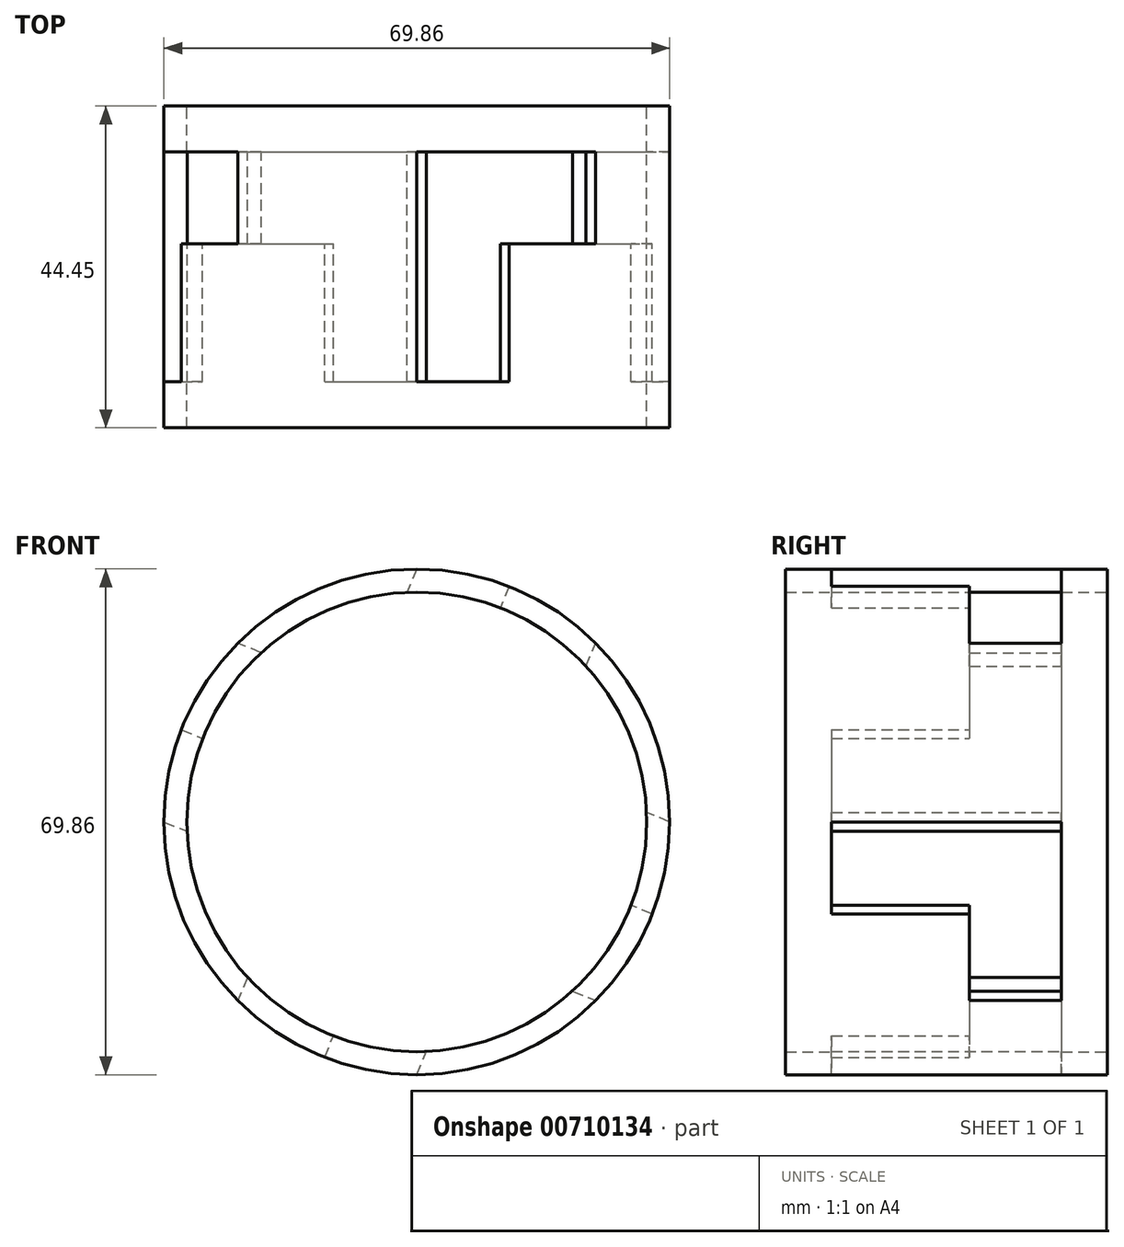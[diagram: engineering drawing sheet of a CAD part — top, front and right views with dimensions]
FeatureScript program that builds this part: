
annotation { "Feature Type Name" : "Feature", "Feature Type Description" : "" }
export const myFeature = defineFeature(function(context is Context, id is Id, definition is map)
    precondition{}
    {
        {
            var Q0;
            Q0=qCreatedBy(makeId("Front.planeOp"),FACE);
            var sketch = newSketch(context, id + "F0", { "sketchPlane" : qUnion([Q0])});
            skCircle(sketch, "E0", {"center": v(0, 0) * mm, "radius": 31.75 * mm});
            skCircle(sketch, "E1", {"center": v(0, 0) * mm, "radius": 34.93 * mm});
            skSolve(sketch);
        }
        {
            var Q0;
            Q0=makeQuery(id+"F0.imprint","IMPRINT",FACE,{"disambiguationData":[TD([[makeQuery(id+"F0.imprint","IMPRINT",EDGE,{"derivedFrom":sQuery(id+"F0.wireOp",EDGE,"E0")}),-1.0]])]});
            extrude(context, id + "F1", {"entities" : qUnion([Q0]), "depth" : 44.45 * mm, "offsetDistance" : 25.4 * mm});
        }
        {
            var Q0;
            Q0=qCreatedBy(makeId("Top.planeOp"),FACE);
            cPlane(context, id + "F2", {"entities" : qUnion([Q0]), "cplaneType" : CPlaneType.OFFSET, "offset" : 38.1 * mm, "width" : 152.4 * mm, "height" : 152.4 * mm});
        }
        {
            var Q0;
            Q0=qCreatedBy(makeId("Front.planeOp"),FACE);
            cPlane(context, id + "F3", {"entities" : qUnion([Q0]), "cplaneType" : CPlaneType.OFFSET, "offset" : 6.35 * mm, "width" : 152.4 * mm, "height" : 152.4 * mm});
        }
        {
            var Q0;
            Q0=qCreatedBy(id+"F3.planeOp",FACE);
            var sketch = newSketch(context, id + "F4", { "sketchPlane" : qUnion([Q0])});
            skLineSegment(sketch, "E2.0", {"start": v(1.22, 37.86) * mm, "end": v(25.91, 27.63) * mm});
            skLineSegment(sketch, "E3.0", {"start": v(-2.43, 29.06) * mm, "end": v(22.27, 18.83) * mm});
            skLineSegment(sketch, "E4", {"start": v(1.22, 37.86) * mm, "end": v(-2.43, 29.06) * mm});
            skLineSegment(sketch, "E5", {"start": v(22.27, 18.83) * mm, "end": v(25.91, 27.63) * mm});
            skLineSegment(sketch, "E6.1.0", {"start": v(-18.83, 22.27) * mm, "end": v(-27.63, 25.91) * mm});
            skLineSegment(sketch, "E6.1.1", {"start": v(-37.86, 1.22) * mm, "end": v(-27.63, 25.91) * mm});
            skLineSegment(sketch, "E6.1.2", {"start": v(-37.86, 1.22) * mm, "end": v(-29.06, -2.43) * mm});
            skLineSegment(sketch, "E6.1.3", {"start": v(-29.06, -2.43) * mm, "end": v(-18.83, 22.27) * mm});
            skLineSegment(sketch, "E6.2.0", {"start": v(-22.27, -18.83) * mm, "end": v(-25.91, -27.63) * mm});
            skLineSegment(sketch, "E6.2.1", {"start": v(-1.22, -37.86) * mm, "end": v(-25.91, -27.63) * mm});
            skLineSegment(sketch, "E6.2.2", {"start": v(-1.22, -37.86) * mm, "end": v(2.43, -29.06) * mm});
            skLineSegment(sketch, "E6.2.3", {"start": v(2.43, -29.06) * mm, "end": v(-22.27, -18.83) * mm});
            skLineSegment(sketch, "E6.3.0", {"start": v(18.83, -22.27) * mm, "end": v(27.63, -25.91) * mm});
            skLineSegment(sketch, "E6.3.1", {"start": v(37.86, -1.22) * mm, "end": v(27.63, -25.91) * mm});
            skLineSegment(sketch, "E6.3.2", {"start": v(37.86, -1.22) * mm, "end": v(29.06, 2.43) * mm});
            skLineSegment(sketch, "E6.3.3", {"start": v(29.06, 2.43) * mm, "end": v(18.83, -22.27) * mm});
            skPoint(sketch, "E6.center", {"position": v(0, 0) * mm});
            skSolve(sketch);
        }
        {
            var Q0;
            Q0=makeQuery(id+"F4.imprint","IMPRINT",FACE,{"disambiguationData":[TD([[makeQuery(id+"F4.imprint","IMPRINT",EDGE,{"derivedFrom":sQuery(id+"F4.wireOp",EDGE,"E6.1.0")}),1.0]])]});
            var Q1;
            Q1=makeQuery(id+"F4.imprint","IMPRINT",FACE,{"disambiguationData":[TD([[makeQuery(id+"F4.imprint","IMPRINT",EDGE,{"derivedFrom":sQuery(id+"F4.wireOp",EDGE,"E2.0")}),-1.0]])]});
            var Q2;
            Q2=makeQuery(id+"F4.imprint","IMPRINT",FACE,{"disambiguationData":[TD([[makeQuery(id+"F4.imprint","IMPRINT",EDGE,{"derivedFrom":sQuery(id+"F4.wireOp",EDGE,"E6.3.0")}),1.0]])]});
            var Q3;
            Q3=makeQuery(id+"F4.imprint","IMPRINT",FACE,{"disambiguationData":[TD([[makeQuery(id+"F4.imprint","IMPRINT",EDGE,{"derivedFrom":sQuery(id+"F4.wireOp",EDGE,"E6.2.0")}),1.0]])]});
            extrude(context, id + "F5", {"entities" : qUnion([Q0, Q1, Q2, Q3]), "operationType" : NewBodyOperationType.REMOVE, "depth" : 12.7 * mm, "offsetDistance" : 25.4 * mm});
        }
        {
            var Q0;
            Q0=qCreatedBy(id+"F3.planeOp",FACE);
            cPlane(context, id + "F6", {"entities" : qUnion([Q0]), "cplaneType" : CPlaneType.OFFSET, "offset" : 12.7 * mm, "width" : 152.4 * mm, "height" : 152.4 * mm});
        }
        {
            var Q0;
            Q0=qCreatedBy(id+"F6.planeOp",FACE);
            var sketch = newSketch(context, id + "F7", { "sketchPlane" : qUnion([Q0])});
            skCircle(sketch, "E7.cCircle", {"center": v(0, 0) * mm, "radius": 34.93 * mm, "construction": true});
            skLineSegment(sketch, "E7.1", {"start": v(24.7, 24.7) * mm, "end": v(34.93, 0) * mm});
            skLineSegment(sketch, "E7.3", {"start": v(24.7, -24.7) * mm, "end": v(0, -34.93) * mm});
            skLineSegment(sketch, "E7.5", {"start": v(-24.7, -24.7) * mm, "end": v(-34.93, 0) * mm});
            skLineSegment(sketch, "E7.7", {"start": v(-24.7, 24.7) * mm, "end": v(0, 34.93) * mm});
            skLineSegment(sketch, "E8.0", {"start": v(-2.43, 29.06) * mm, "end": v(9.3, 24.2) * mm});
            skLineSegment(sketch, "E9.0", {"start": v(1.22, 37.86) * mm, "end": v(12.95, 33) * mm});
            skLineSegment(sketch, "E10", {"start": v(1.22, 37.86) * mm, "end": v(-2.43, 29.06) * mm});
            skLineSegment(sketch, "E11.0", {"start": v(12.95, 33) * mm, "end": v(9.3, 24.2) * mm});
            skLineSegment(sketch, "E12.1.0", {"start": v(-29.06, -2.43) * mm, "end": v(-24.2, 9.3) * mm});
            skLineSegment(sketch, "E12.1.1", {"start": v(-33, 12.95) * mm, "end": v(-24.2, 9.3) * mm});
            skLineSegment(sketch, "E12.1.2", {"start": v(-37.86, 1.22) * mm, "end": v(-29.06, -2.43) * mm});
            skLineSegment(sketch, "E12.1.3", {"start": v(-37.86, 1.22) * mm, "end": v(-33, 12.95) * mm});
            skLineSegment(sketch, "E12.2.0", {"start": v(2.43, -29.06) * mm, "end": v(-9.3, -24.2) * mm});
            skLineSegment(sketch, "E12.2.1", {"start": v(-12.95, -33) * mm, "end": v(-9.3, -24.2) * mm});
            skLineSegment(sketch, "E12.2.2", {"start": v(-1.22, -37.86) * mm, "end": v(2.43, -29.06) * mm});
            skLineSegment(sketch, "E12.2.3", {"start": v(-1.22, -37.86) * mm, "end": v(-12.95, -33) * mm});
            skLineSegment(sketch, "E12.3.0", {"start": v(29.06, 2.43) * mm, "end": v(24.2, -9.3) * mm});
            skLineSegment(sketch, "E12.3.1", {"start": v(33, -12.95) * mm, "end": v(24.2, -9.3) * mm});
            skLineSegment(sketch, "E12.3.2", {"start": v(37.86, -1.22) * mm, "end": v(29.06, 2.43) * mm});
            skLineSegment(sketch, "E12.3.3", {"start": v(37.86, -1.22) * mm, "end": v(33, -12.95) * mm});
            skSolve(sketch);
        }
        {
            var Q0;
            {var subQ2=sQuery(id+"F7.wireOp",EDGE,"E8.0");Q0=makeQuery(id+"F7.imprint","IMPRINT",FACE,{"disambiguationData":[TD([[makeQuery(id+"F7.imprint","IMPRINT",EDGE,{"derivedFrom":subQ2}),1.0]])]});}
            var Q1;
            {var subQ2=sQuery(id+"F7.wireOp",EDGE,"E12.1.0");Q1=makeQuery(id+"F7.imprint","IMPRINT",FACE,{"disambiguationData":[TD([[makeQuery(id+"F7.imprint","IMPRINT",EDGE,{"derivedFrom":subQ2}),1.0]])]});}
            var Q2;
            {var subQ2=sQuery(id+"F7.wireOp",EDGE,"E12.2.0");Q2=makeQuery(id+"F7.imprint","IMPRINT",FACE,{"disambiguationData":[TD([[makeQuery(id+"F7.imprint","IMPRINT",EDGE,{"derivedFrom":subQ2}),1.0]])]});}
            var Q3;
            {var subQ2=sQuery(id+"F7.wireOp",EDGE,"E12.3.0");Q3=makeQuery(id+"F7.imprint","IMPRINT",FACE,{"disambiguationData":[TD([[makeQuery(id+"F7.imprint","IMPRINT",EDGE,{"derivedFrom":subQ2}),1.0]])]});}
            extrude(context, id + "F8", {"entities" : qUnion([Q0, Q1, Q2, Q3]), "operationType" : NewBodyOperationType.REMOVE, "depth" : 19.05 * mm, "offsetDistance" : 25.4 * mm});
        }
    });
